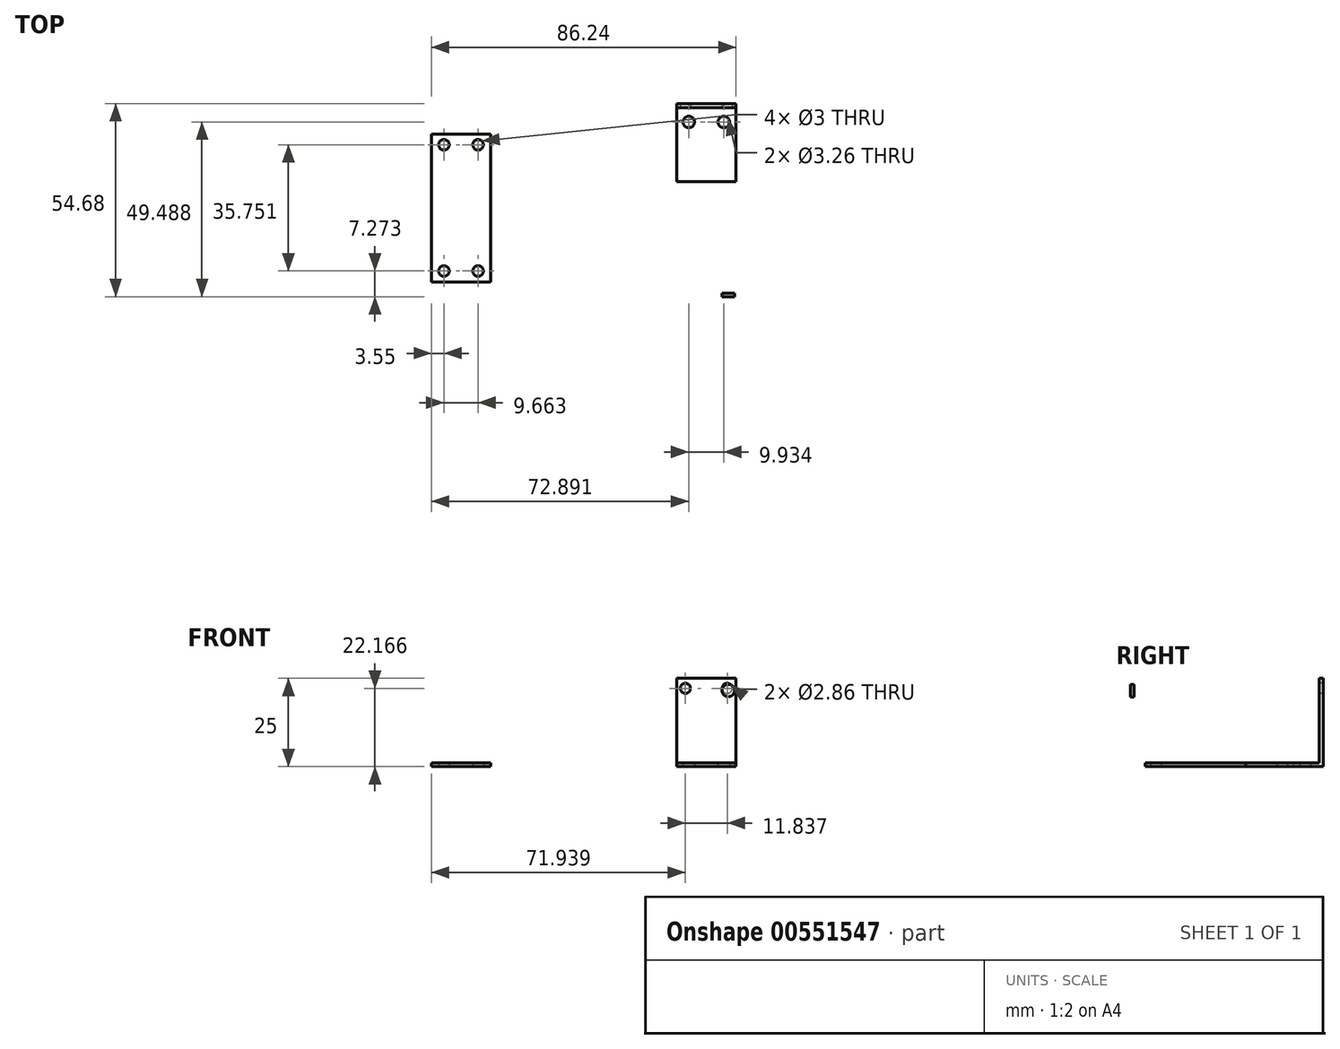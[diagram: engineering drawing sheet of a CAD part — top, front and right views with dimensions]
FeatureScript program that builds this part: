
annotation { "Feature Type Name" : "Feature", "Feature Type Description" : "" }
export const myFeature = defineFeature(function(context is Context, id is Id, definition is map)
    precondition{}
    {
        {
            var Q0;
            Q0=qCreatedBy(makeId("Top.planeOp"),FACE);
            var sketch = newSketch(context, id + "F0", { "sketchPlane" : qUnion([Q0])});
            skLineSegment(sketch, "E0.bottom", {"start": v(-53.27, 17.7) * mm, "end": v(-36.5, 17.7) * mm});
            skLineSegment(sketch, "E0.top", {"start": v(-53.27, -24.23) * mm, "end": v(-36.5, -24.23) * mm});
            skLineSegment(sketch, "E0.left", {"start": v(-53.27, 17.7) * mm, "end": v(-53.27, -24.23) * mm});
            skLineSegment(sketch, "E0.right", {"start": v(-36.5, 17.7) * mm, "end": v(-36.5, -24.23) * mm});
            skLineSegment(sketch, "E1", {"start": v(-44.89, -24.23) * mm, "end": v(-44.89, 17.7) * mm, "construction": true});
            skLineSegment(sketch, "E2", {"start": v(-36.5, -3.27) * mm, "end": v(-53.27, -3.27) * mm, "construction": true});
            skLineSegment(sketch, "E3.bottom", {"start": v(16.2, 26.26) * mm, "end": v(32.97, 26.26) * mm});
            skLineSegment(sketch, "E3.top", {"start": v(16.2, 4.22) * mm, "end": v(32.97, 4.22) * mm});
            skLineSegment(sketch, "E3.left", {"start": v(16.2, 26.26) * mm, "end": v(16.2, 4.22) * mm});
            skLineSegment(sketch, "E3.right", {"start": v(32.97, 26.26) * mm, "end": v(32.97, 4.22) * mm});
            skLineSegment(sketch, "E4", {"start": v(16.2, 25.1) * mm, "end": v(32.97, 25.1) * mm});
            skCircle(sketch, "E5", {"center": v(-49.72, 14.6) * mm, "radius": 1.5 * mm});
            skCircle(sketch, "E6.MirrorC", {"center": v(-49.72, -21.15) * mm, "radius": 1.5 * mm});
            skCircle(sketch, "E7.MirrorC", {"center": v(-40.06, 14.6) * mm, "radius": 1.5 * mm});
            skCircle(sketch, "E8.MirrorC", {"center": v(-40.06, -21.15) * mm, "radius": 1.5 * mm});
            skCircle(sketch, "E9", {"center": v(19.62, 21.07) * mm, "radius": 1.63 * mm});
            skLineSegment(sketch, "E10", {"start": v(24.59, 25.1) * mm, "end": v(24.59, 4.22) * mm, "construction": true});
            skCircle(sketch, "E11.MirrorC", {"center": v(29.55, 21.07) * mm, "radius": 1.63 * mm});
            skLineSegment(sketch, "E12.top", {"start": v(16.3, -27.42) * mm, "end": v(33.06, -27.42) * mm});
            skLineSegment(sketch, "E12.left", {"start": v(16.3, -6.53) * mm, "end": v(16.3, -27.42) * mm});
            skLineSegment(sketch, "E12.right", {"start": v(33.06, -6.53) * mm, "end": v(33.06, -27.42) * mm});
            skLineSegment(sketch, "E13", {"start": v(16.3, -6.53) * mm, "end": v(33.06, -6.53) * mm});
            skCircle(sketch, "E14", {"center": v(19.71, -10.57) * mm, "radius": 1.63 * mm});
            skLineSegment(sketch, "E15", {"start": v(24.68, -6.53) * mm, "end": v(24.68, -27.42) * mm, "construction": true});
            skCircle(sketch, "E16.MirrorC", {"center": v(29.64, -10.57) * mm, "radius": 1.63 * mm});
            skLineSegment(sketch, "E17.bottom", {"start": v(16.3, -27.42) * mm, "end": v(33.2, -27.42) * mm});
            skLineSegment(sketch, "E17.top", {"start": v(16.3, -28.42) * mm, "end": v(33.2, -28.42) * mm});
            skLineSegment(sketch, "E17.left", {"start": v(16.3, -27.42) * mm, "end": v(16.3, -28.42) * mm});
            skLineSegment(sketch, "E17.right", {"start": v(33.2, -27.42) * mm, "end": v(33.2, -28.42) * mm});
            skSolve(sketch);
        }
        {
            var Q0;
            {var subQ0=sQuery(id+"F0.wireOp",EDGE,"E3.top");Q0=makeQuery(id+"F0.imprint","IMPRINT",FACE,{"disambiguationData":[TD([[makeQuery(id+"F0.imprint","IMPRINT",EDGE,{"derivedFrom":subQ0}),1.0]])]});}
            extrude(context, id + "F1", {"entities" : qUnion([Q0]), "depth" : 1 * mm, "offsetDistance" : 25 * mm});
        }
        {
            var Q0;
            {var subQ0=sQuery(id+"F0.wireOp",EDGE,"E3.bottom");Q0=makeQuery(id+"F0.imprint","IMPRINT",FACE,{"disambiguationData":[TD([[makeQuery(id+"F0.imprint","IMPRINT",EDGE,{"derivedFrom":subQ0}),-1.0]])]});}
            extrude(context, id + "F2", {"entities" : qUnion([Q0]), "operationType" : NewBodyOperationType.ADD, "depth" : 25 * mm, "offsetDistance" : 25 * mm});
        }
        {
            var Q0;
            Q0=makeQuery(id+"F0.imprint","IMPRINT",FACE,{"disambiguationData":[TD([[makeQuery(id+"F0.imprint","IMPRINT",EDGE,{"derivedFrom":sQuery(id+"F0.wireOp",EDGE,"E0.bottom")}),-1.0]])]});
            extrude(context, id + "F3", {"entities" : qUnion([Q0]), "depth" : 1 * mm, "offsetDistance" : 25 * mm});
        }
        {
            var Q0;
            Q0=makeQuery(id+"F2.opExtrude","SWEPT_FACE",FACE,{"disambiguationData":[OSD([sQuery(id+"F0.wireOp",EDGE,"E3.bottom")])]});
            var sketch = newSketch(context, id + "F4", { "sketchPlane" : qUnion([Q0])});
            skCircle(sketch, "E18", {"center": v(-38.53, 21.38) * mm, "radius": 1.38 * mm});
            skLineSegment(sketch, "E19", {"start": v(-24.59, 25) * mm, "end": v(-24.59, 0) * mm});
            skCircle(sketch, "E20.MirrorC", {"center": v(-10.64, 21.38) * mm, "radius": 1.38 * mm});
            skSolve(sketch);
        }
        {
            var Q0;
            Q0 = qSketchRegion(id + "F4", true);
            extrude(context, id + "F5", {"entities" : qUnion([Q0]), "operationType" : NewBodyOperationType.REMOVE, "oppositeDirection" : true, "depth" : 25 * mm, "offsetDistance" : 25 * mm});
        }
        {
            var Q0;
            {var subQ1=sQuery(id+"F0.wireOp",EDGE,"E12.left");Q0=makeQuery(id+"F0.imprint","IMPRINT",FACE,{"disambiguationData":[TD([[makeQuery(id+"F0.imprint","IMPRINT",EDGE,{"derivedFrom":subQ1}),1.0]])]});}
            extrude(context, id + "F6", {"entities" : qUnion([Q0]), "depth" : 1 * mm, "offsetDistance" : 25 * mm});
        }
        {
            var Q0;
            Q0=makeQuery(id+"F0.imprint","IMPRINT",FACE,{"disambiguationData":[TD([[makeQuery(id+"F0.imprint","IMPRINT",EDGE,{"derivedFrom":sQuery(id+"F0.wireOp",EDGE,"E17.top")}),1.0]])]});
            extrude(context, id + "F7", {"entities" : qUnion([Q0]), "operationType" : NewBodyOperationType.ADD, "depth" : 25 * mm, "offsetDistance" : 25 * mm});
        }
        {
            var Q0;
            Q0=makeQuery(id+"F7.opExtrude","SWEPT_FACE",FACE,{"disambiguationData":[OSD([sQuery(id+"F0.wireOp",EDGE,"E17.top")])]});
            var sketch = newSketch(context, id + "F8", { "sketchPlane" : qUnion([Q0])});
            skCircle(sketch, "E21", {"center": v(18.69, 21.52) * mm, "radius": 1.76 * mm});
            skLineSegment(sketch, "E22", {"start": v(24.75, 25) * mm, "end": v(24.75, 0) * mm, "construction": true});
            skCircle(sketch, "E23.MirrorC", {"center": v(30.81, 21.52) * mm, "radius": 1.76 * mm});
            skSolve(sketch);
        }
        {
            var Q0;
            Q0=makeQuery(id+"F8.imprint","IMPRINT",FACE,{"disambiguationData":[TD([[makeQuery(id+"F8.imprint","IMPRINT",EDGE,{"derivedFrom":sQuery(id+"F8.wireOp",EDGE,"E21")}),1.0]])]});
            var Q1;
            Q1=makeQuery(id+"F8.imprint","IMPRINT",FACE,{"disambiguationData":[TD([[makeQuery(id+"F8.imprint","IMPRINT",EDGE,{"derivedFrom":sQuery(id+"F8.wireOp",EDGE,"E23.MirrorC")}),-1.0]])]});
            var Q2;
            Q2=sQuery(id+"F8.wireOp",EDGE,"E21");
            var Q3;
            Q3=sQuery(id+"F8.wireOp",EDGE,"E23.MirrorC");
            extrude(context, id + "F9", {"entities" : qUnion([Q0, Q1]), "operationType" : NewBodyOperationType.REMOVE, "surfaceEntities" : qUnion([Q2, Q3]), "oppositeDirection" : true, "depth" : 25 * mm, "offsetDistance" : 25 * mm});
        }
        {
            var Q0;
            Q0=makeQuery(id+"F2.opExtrude","SWEPT_FACE",FACE,{"disambiguationData":[OSD([sQuery(id+"F0.wireOp",EDGE,"E4")])]});
            var sketch = newSketch(context, id + "F10", { "sketchPlane" : qUnion([Q0])});
            skCircle(sketch, "E24", {"center": v(18.67, 22.17) * mm, "radius": 1.43 * mm});
            skLineSegment(sketch, "E25", {"start": v(24.59, 25) * mm, "end": v(24.59, 1) * mm, "construction": true});
            skCircle(sketch, "E26.MirrorC", {"center": v(30.5, 22.17) * mm, "radius": 1.43 * mm});
            skSolve(sketch);
        }
        {
            var Q0;
            Q0 = qSketchRegion(id + "F10", true);
            extrude(context, id + "F11", {"entities" : qUnion([Q0]), "operationType" : NewBodyOperationType.REMOVE, "oppositeDirection" : true, "depth" : 25 * mm, "offsetDistance" : 25 * mm});
        }
    });
